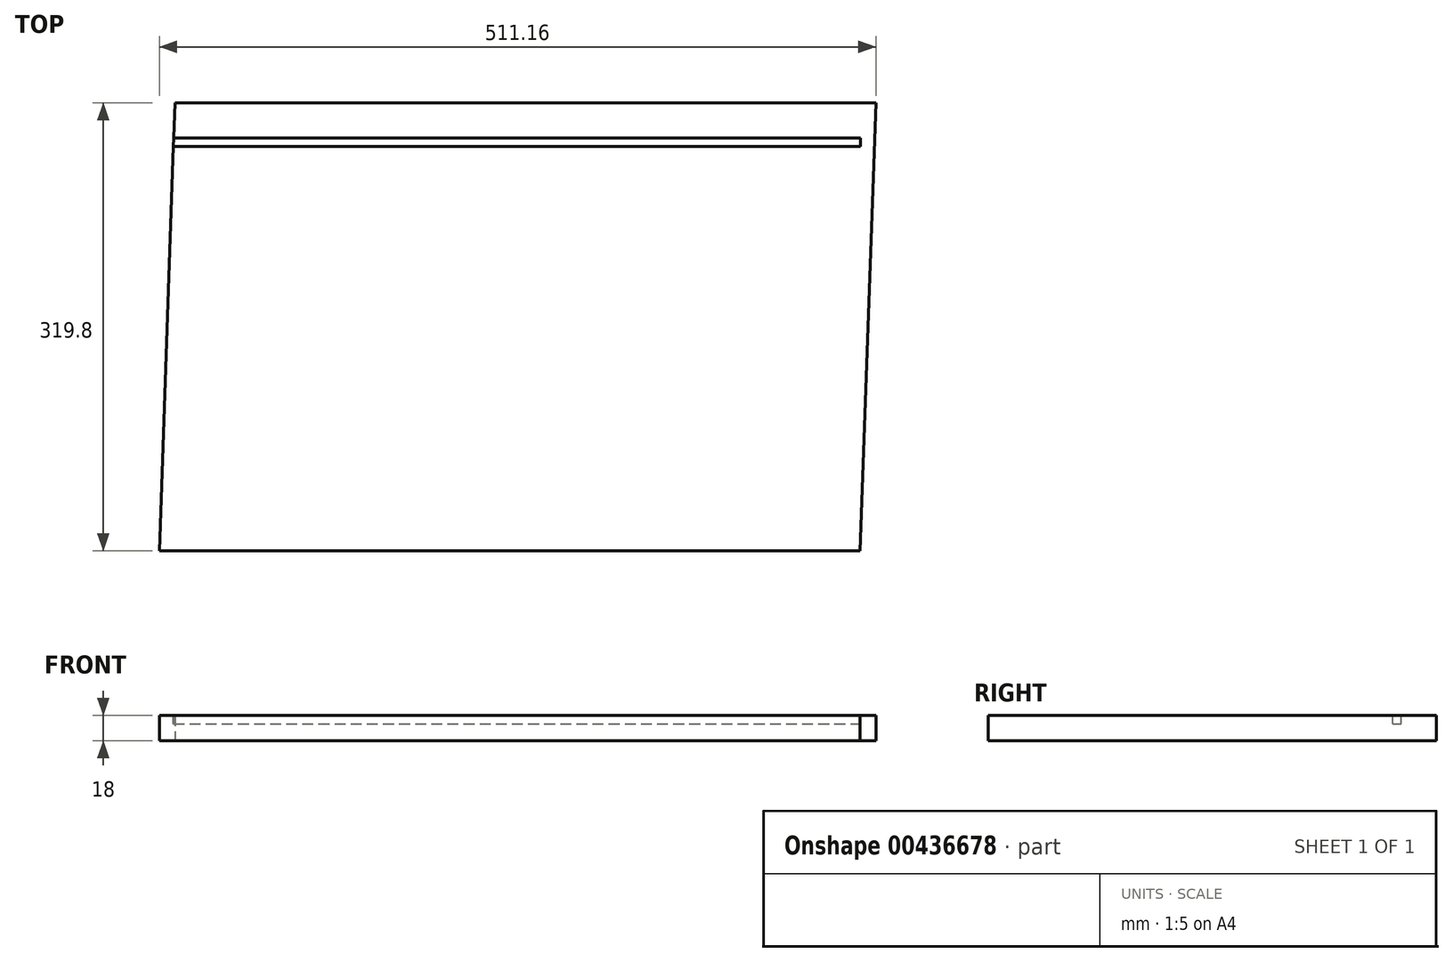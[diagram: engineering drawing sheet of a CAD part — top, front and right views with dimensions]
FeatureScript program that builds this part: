
annotation { "Feature Type Name" : "Feature", "Feature Type Description" : "" }
export const myFeature = defineFeature(function(context is Context, id is Id, definition is map)
    precondition{}
    {
        {
            var Q0;
            Q0=qCreatedBy(makeId("Top.planeOp"),FACE);
            var sketch = newSketch(context, id + "F0", { "sketchPlane" : qUnion([Q0])});
            skLineSegment(sketch, "E0.bottom", {"start": v(244.42, -159.9) * mm, "end": v(-255.58, -159.9) * mm});
            skLineSegment(sketch, "E0.top", {"start": v(255.58, 159.9) * mm, "end": v(-244.42, 159.9) * mm});
            skLineSegment(sketch, "E0.left", {"start": v(244.42, -159.9) * mm, "end": v(255.58, 159.9) * mm});
            skLineSegment(sketch, "E0.right", {"start": v(-255.58, -159.9) * mm, "end": v(-244.42, 159.9) * mm});
            skPoint(sketch, "E0.middle", {"position": v(0, 0) * mm});
            skSolve(sketch);
        }
        {
            var Q0;
            Q0=qSketchRegion(id+"F0",true);
            extrude(context, id + "F1", {"entities" : qUnion([Q0]), "depth" : 18 * mm});
        }
        {
            var Q0;
            Q0=makeQuery(id+"F1.opExtrude","CAP_FACE",FACE,{"disambiguationData":[OSD([sQuery(id+"F0.wireOp",EDGE,"E0.bottom"),sQuery(id+"F0.wireOp",EDGE,"E0.top"),sQuery(id+"F0.wireOp",EDGE,"E0.left"),sQuery(id+"F0.wireOp",EDGE,"E0.right")])],"isStart":false});
            var sketch = newSketch(context, id + "F2", { "sketchPlane" : qUnion([Q0])});
            skLineSegment(sketch, "E1.bottom", {"start": v(-245.29, 134.9) * mm, "end": v(244.5, 134.9) * mm});
            skLineSegment(sketch, "E1.top", {"start": v(-245.5, 128.9) * mm, "end": v(244.5, 128.9) * mm});
            skLineSegment(sketch, "E2", {"start": v(-245.29, 134.9) * mm, "end": v(-245.5, 128.9) * mm});
            skLineSegment(sketch, "E3", {"start": v(244.5, 134.9) * mm, "end": v(244.5, 128.9) * mm});
            skSolve(sketch);
        }
        {
            var Q0;
            Q0=qSketchRegion(id+"F2",true);
            extrude(context, id + "F3", {"entities" : qUnion([Q0]), "operationType" : NewBodyOperationType.REMOVE, "oppositeDirection" : true, "depth" : 6 * mm});
        }
    });
